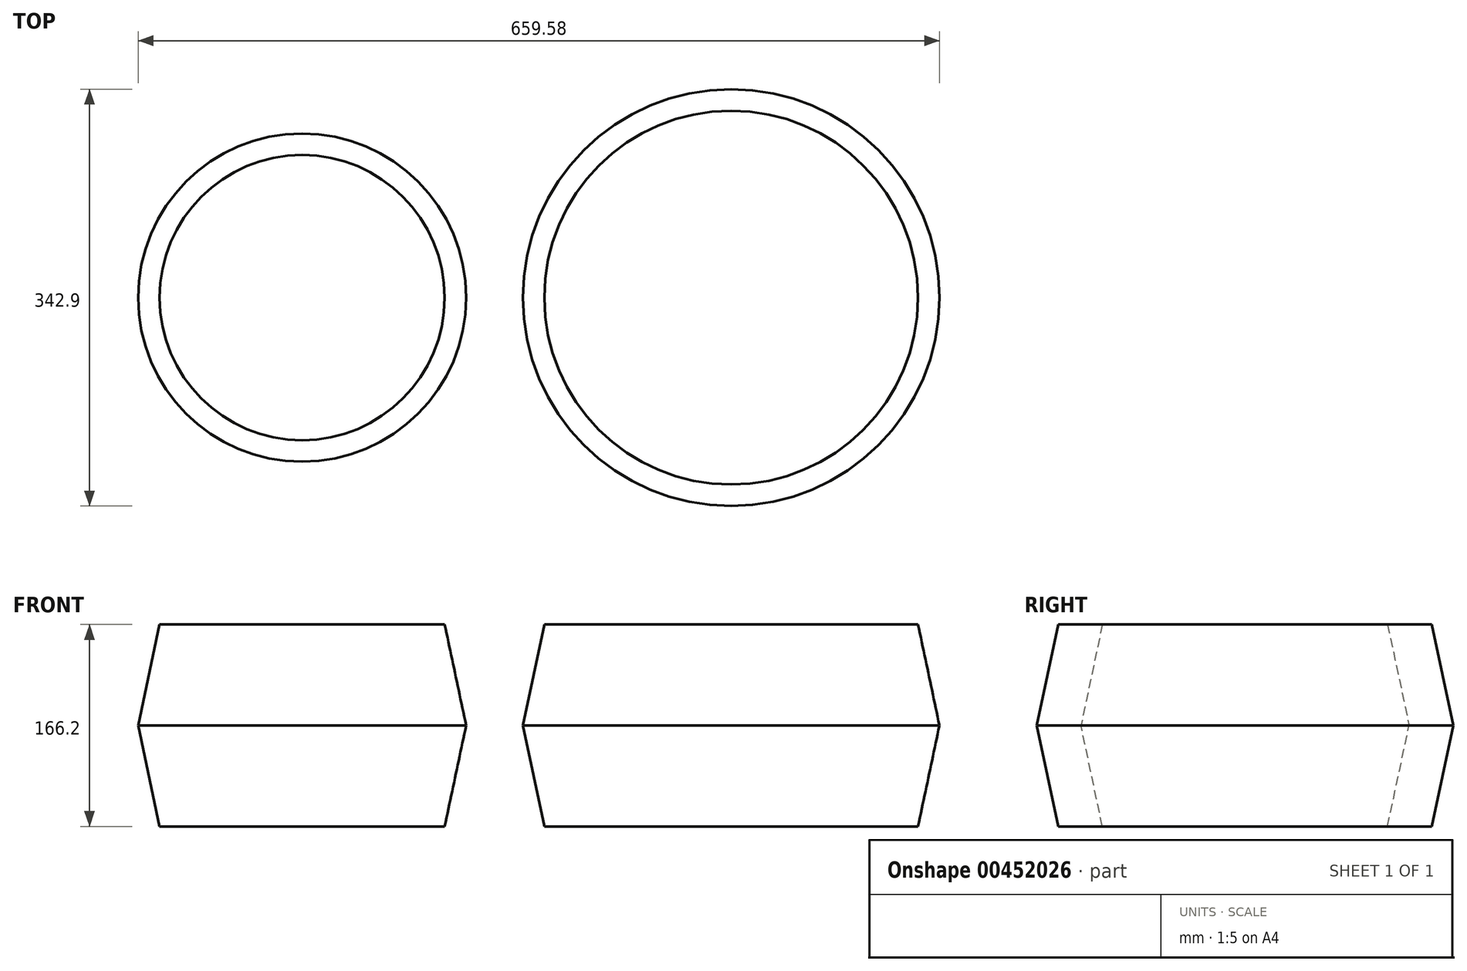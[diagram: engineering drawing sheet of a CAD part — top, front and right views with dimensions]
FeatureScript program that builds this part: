
annotation { "Feature Type Name" : "Feature", "Feature Type Description" : "" }
export const myFeature = defineFeature(function(context is Context, id is Id, definition is map)
    precondition{}
    {
        {
            var Q0;
            Q0=qCreatedBy(makeId("Top.planeOp"),FACE);
            var sketch = newSketch(context, id + "F0", { "sketchPlane" : qUnion([Q0])});
            skCircle(sketch, "E0", {"center": v(0, 0) * mm, "radius": 135 * mm});
            skCircle(sketch, "E1", {"center": v(353.13, 0) * mm, "radius": 171.45 * mm});
            skSolve(sketch);
        }
        {
            var Q0;
            Q0 = qSketchRegion(id + "F0", true);
            extrude(context, id + "F1", {"entities" : qUnion([Q0]), "endBound" : BoundingType.SYMMETRIC, "depth" : 166.2 * mm, "offsetDistance" : 25.4 * mm, "hasDraft" : true, "draftAngle" : 12 * degree, "draftPullDirection" : true});
        }
    });
